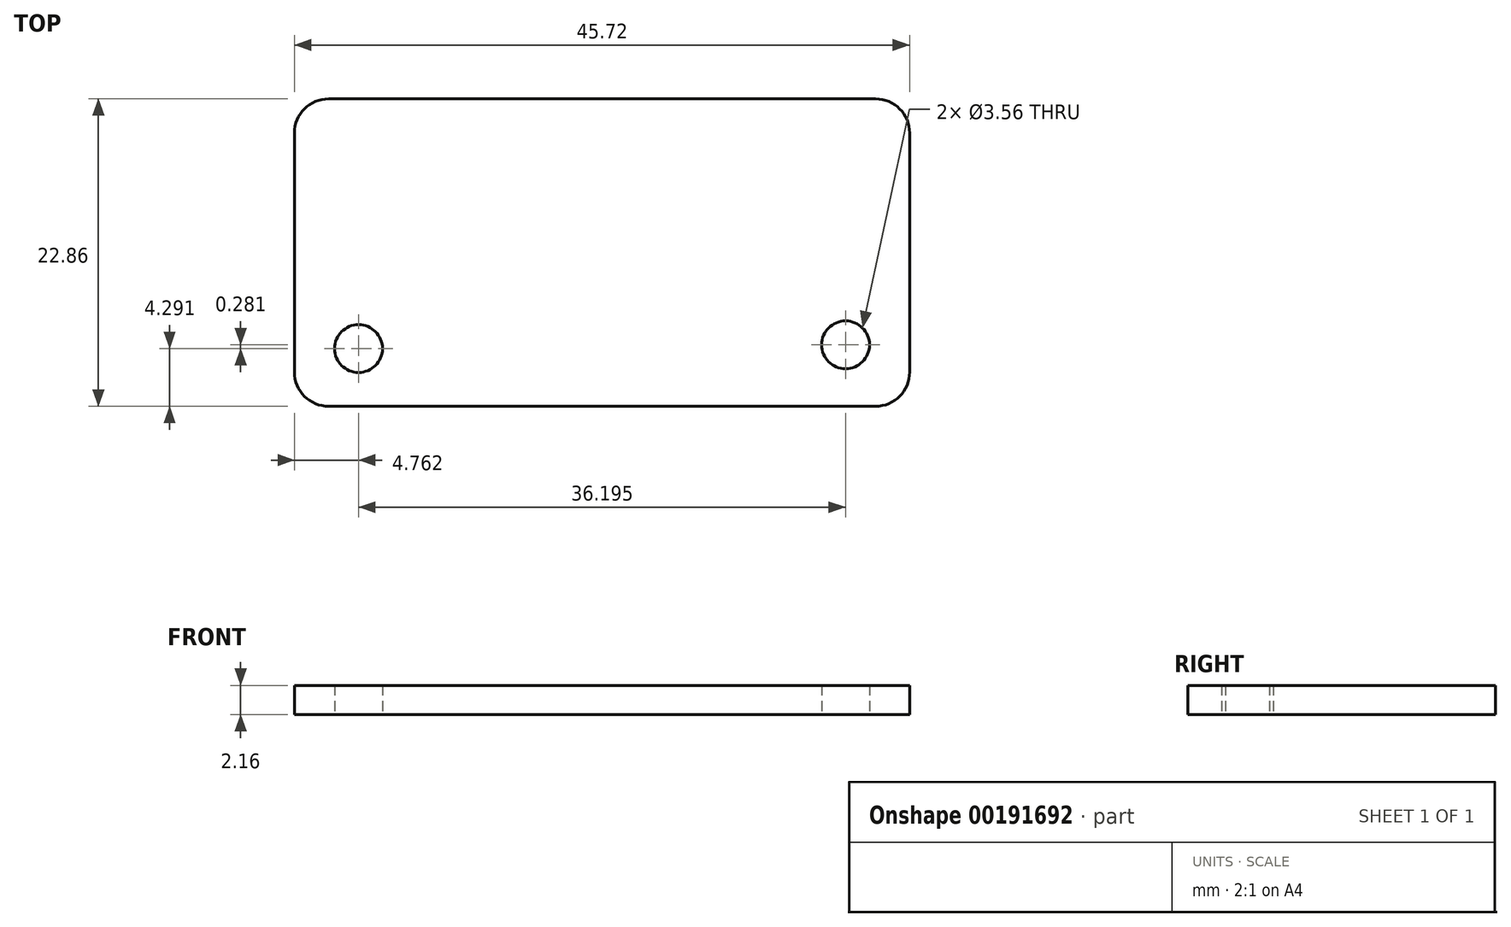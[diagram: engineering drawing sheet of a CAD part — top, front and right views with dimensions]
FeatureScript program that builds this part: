
annotation { "Feature Type Name" : "Feature", "Feature Type Description" : "" }
export const myFeature = defineFeature(function(context is Context, id is Id, definition is map)
    precondition{}
    {
        {
            var Q0;
            Q0=qCreatedBy(makeId("Top.planeOp"),FACE);
            var sketch = newSketch(context, id + "F0", { "sketchPlane" : qUnion([Q0])});
            skLineSegment(sketch, "E0.bottom", {"start": v(22.86, 11.43) * mm, "end": v(-22.86, 11.43) * mm});
            skLineSegment(sketch, "E0.top", {"start": v(22.86, -11.43) * mm, "end": v(-22.86, -11.43) * mm});
            skLineSegment(sketch, "E0.left", {"start": v(22.86, 11.43) * mm, "end": v(22.86, -11.43) * mm});
            skLineSegment(sketch, "E0.right", {"start": v(-22.86, 11.43) * mm, "end": v(-22.86, -11.43) * mm});
            skPoint(sketch, "E0.middle", {"position": v(0, 0) * mm});
            skCircle(sketch, "E1", {"center": v(-18.1, -7.14) * mm, "radius": 1.78 * mm});
            skCircle(sketch, "E2", {"center": v(18.1, -6.86) * mm, "radius": 1.78 * mm});
            skSolve(sketch);
        }
        {
            var Q0;
            Q0 = qSketchRegion(id + "F0", true);
            extrude(context, id + "F1", {"entities" : qUnion([Q0]), "depth" : 2.16 * mm});
        }
        {
            var Q0;
            Q0=makeQuery(id+"F1.opExtrude","SWEPT_EDGE",EDGE,{"disambiguationData":[OSD([sQuery(id+"F0.wireOp",EDGE,"E0.top"),sQuery(id+"F0.wireOp",EDGE,"E0.left")])]});
            var Q1;
            Q1=makeQuery(id+"F1.opExtrude","SWEPT_EDGE",EDGE,{"disambiguationData":[OSD([sQuery(id+"F0.wireOp",EDGE,"E0.bottom"),sQuery(id+"F0.wireOp",EDGE,"E0.left")])]});
            var Q2;
            Q2=makeQuery(id+"F1.opExtrude","SWEPT_EDGE",EDGE,{"disambiguationData":[OSD([sQuery(id+"F0.wireOp",EDGE,"E0.top"),sQuery(id+"F0.wireOp",EDGE,"E0.right")])]});
            var Q3;
            Q3=makeQuery(id+"F1.opExtrude","SWEPT_EDGE",EDGE,{"disambiguationData":[OSD([sQuery(id+"F0.wireOp",EDGE,"E0.bottom"),sQuery(id+"F0.wireOp",EDGE,"E0.right")])]});
            fillet(context, id + "F2", {"entities" : qUnion([Q0, Q1, Q2, Q3]), "radius" : 2.54 * mm, "tangentPropagation" : true, "allowEdgeOverflow" : false});
        }
    });
